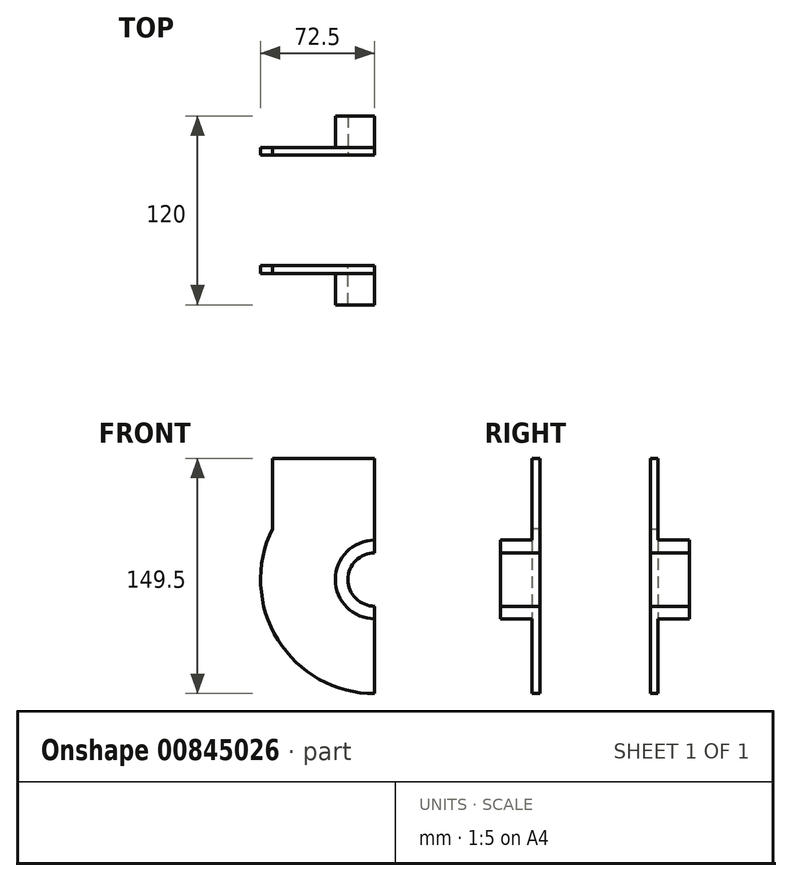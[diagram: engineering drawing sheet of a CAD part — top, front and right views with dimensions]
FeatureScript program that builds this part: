
annotation { "Feature Type Name" : "Feature", "Feature Type Description" : "" }
export const myFeature = defineFeature(function(context is Context, id is Id, definition is map)
    precondition{}
    {
        {
            var Q0;
            Q0=qCreatedBy(makeId("Front.planeOp"),FACE);
            var sketch = newSketch(context, id + "F0", { "sketchPlane" : qUnion([Q0])});
            skArc(sketch, "E0", {"start": v(0, 25) * mm, "mid": v(-25, 0) * mm, "end": v(0, -25) * mm});
            skArc(sketch, "E1", {"start": v(0, 17) * mm, "mid": v(-17, 0) * mm, "end": v(0, -17) * mm});
            skLineSegment(sketch, "E2", {"start": v(0, 25) * mm, "end": v(0, 17) * mm});
            skLineSegment(sketch, "E3.trimOffspring", {"start": v(0, -17) * mm, "end": v(0, -25) * mm});
            skSolve(sketch);
        }
        {
            var Q0;
            Q0 = qSketchRegion(id + "F0", true);
            extrude(context, id + "F1", {"entities" : qUnion([Q0]), "depth" : 20 * mm, "offsetDistance" : 25 * mm, "hasSecondDirection" : true, "secondDirectionOppositeDirection" : true, "secondDirectionDepth" : 5 * mm});
        }
        {
            var Q0;
            Q0=qCreatedBy(makeId("Front.planeOp"),FACE);
            var sketch = newSketch(context, id + "F2", { "sketchPlane" : qUnion([Q0])});
            skArc(sketch, "E4", {"start": v(-65, 32.11) * mm, "mid": v(-61.58, -38.26) * mm, "end": v(0, -72.5) * mm});
            skLineSegment(sketch, "E5", {"start": v(0, 25) * mm, "end": v(0, 77) * mm});
            skLineSegment(sketch, "E6", {"start": v(0, 77) * mm, "end": v(-65, 77) * mm});
            skLineSegment(sketch, "E7", {"start": v(0, -25) * mm, "end": v(0, -72.5) * mm});
            skLineSegment(sketch, "E8", {"start": v(-65, 77) * mm, "end": v(-65, 32.11) * mm});
            skArc(sketch, "E9", {"start": v(0, 25) * mm, "mid": v(-25, 0) * mm, "end": v(0, -25) * mm});
            skSolve(sketch);
        }
        {
            var Q0;
            Q0 = qSketchRegion(id + "F2", true);
            extrude(context, id + "F3", {"entities" : qUnion([Q0]), "operationType" : NewBodyOperationType.ADD, "oppositeDirection" : true, "depth" : 5 * mm, "offsetDistance" : 25 * mm});
        }
        {
            var Q0;
            Q0=qCreatedBy(makeId("Front.planeOp"),FACE);
            cPlane(context, id + "F4", {"entities" : qUnion([Q0]), "cplaneType" : CPlaneType.OFFSET, "offset" : 40 * mm, "oppositeDirection" : true, "width" : 150 * mm, "height" : 150 * mm});
        }
        {
            var Q0;
            Q0=makeQuery(id+"F1.opExtrude","SWEPT_BODY",BODY,{"disambiguationData":[OSD([sQuery(id+"F0.wireOp",EDGE,"E0"),sQuery(id+"F0.wireOp",EDGE,"E1"),sQuery(id+"F0.wireOp",EDGE,"E2"),sQuery(id+"F0.wireOp",EDGE,"E3.trimOffspring")])]});
            var Q1;
            Q1=qCreatedBy(id+"F4.planeOp",FACE);
            mirror(context, id + "F5", {"entities" : qUnion([Q0]), "mirrorPlane" : qUnion([Q1])});
        }
    });
